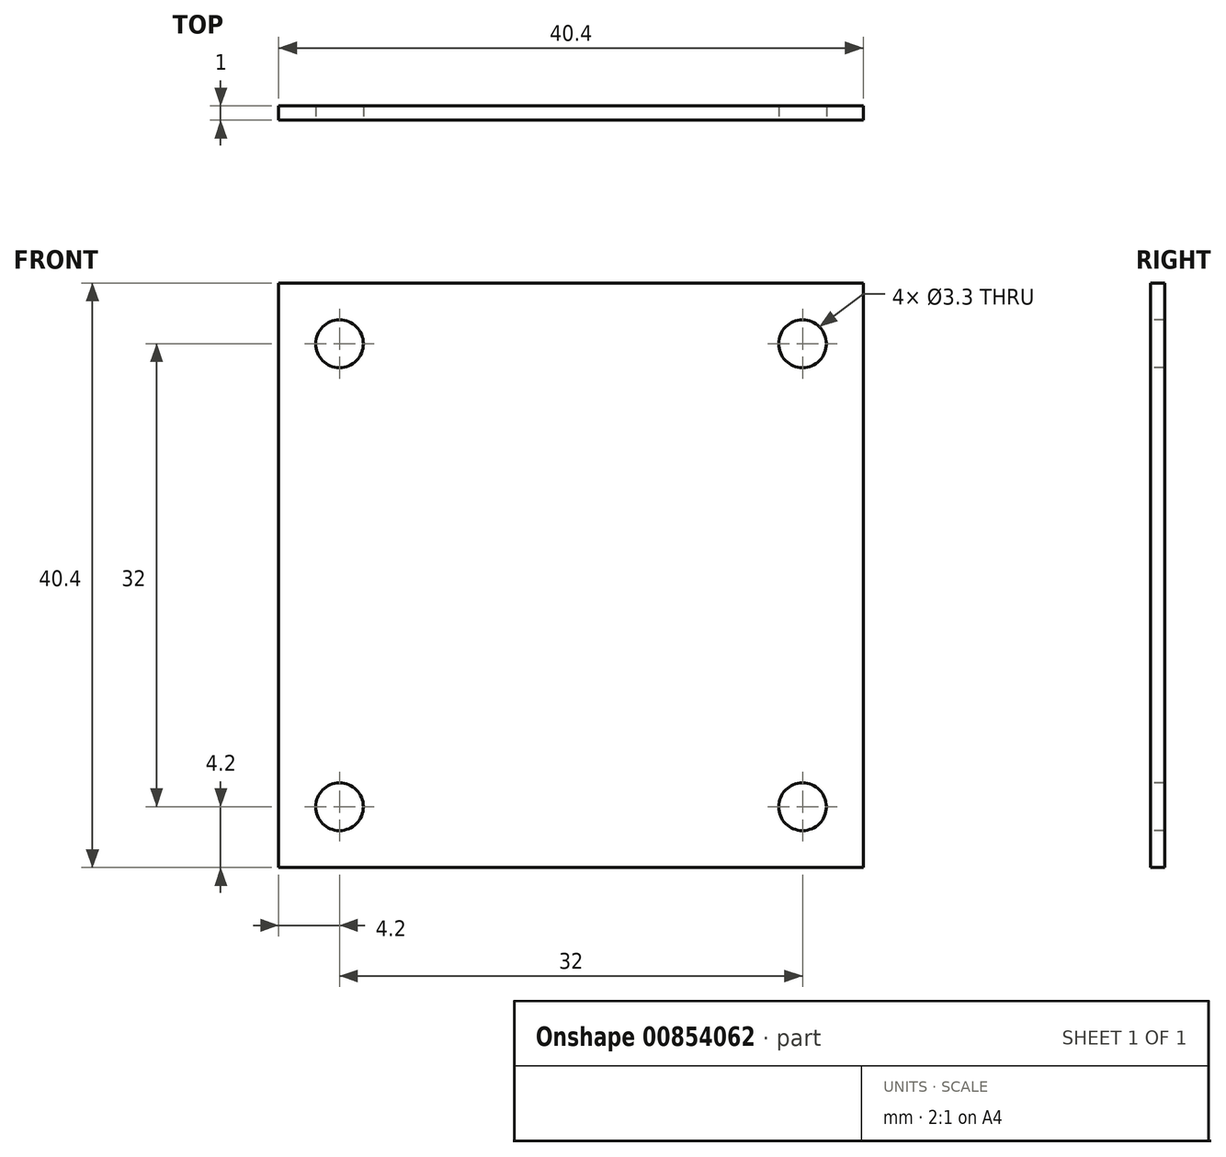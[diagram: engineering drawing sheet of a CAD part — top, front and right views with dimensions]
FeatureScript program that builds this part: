
annotation { "Feature Type Name" : "Feature", "Feature Type Description" : "" }
export const myFeature = defineFeature(function(context is Context, id is Id, definition is map)
    precondition{}
    {
        {
            var Q0;
            Q0=qCreatedBy(makeId("Front.planeOp"),FACE);
            var sketch = newSketch(context, id + "F0", { "sketchPlane" : qUnion([Q0])});
            skLineSegment(sketch, "E0.bottom", {"start": v(0, 0) * mm, "end": v(40.4, 0) * mm});
            skLineSegment(sketch, "E0.top", {"start": v(0, 40.4) * mm, "end": v(40.4, 40.4) * mm});
            skLineSegment(sketch, "E0.left", {"start": v(0, 0) * mm, "end": v(0, 40.4) * mm});
            skLineSegment(sketch, "E0.right", {"start": v(40.4, 0) * mm, "end": v(40.4, 40.4) * mm});
            skSolve(sketch);
        }
        {
            var Q0;
            Q0=makeQuery(id+"F0.imprint","IMPRINT",FACE,{"disambiguationData":[TD([[makeQuery(id+"F0.imprint","IMPRINT",EDGE,{"derivedFrom":sQuery(id+"F0.wireOp",EDGE,"E0.bottom")}),1.0]])]});
            extrude(context, id + "F1", {"entities" : qUnion([Q0]), "depth" : 1 * mm, "offsetDistance" : 25 * mm});
        }
        {
            var Q0;
            Q0=makeQuery(id+"F1.opExtrude","CAP_FACE",FACE,{"disambiguationData":[OSD([sQuery(id+"F0.wireOp",EDGE,"E0.bottom"),sQuery(id+"F0.wireOp",EDGE,"E0.top"),sQuery(id+"F0.wireOp",EDGE,"E0.left"),sQuery(id+"F0.wireOp",EDGE,"E0.right")])],"isStart":false});
            var sketch = newSketch(context, id + "F2", { "sketchPlane" : qUnion([Q0])});
            skPoint(sketch, "E1", {"position": v(36.2, 36.2) * mm});
            skPoint(sketch, "E2", {"position": v(4.2, 36.2) * mm});
            skPoint(sketch, "E3", {"position": v(4.2, 4.2) * mm});
            skPoint(sketch, "E4", {"position": v(36.2, 4.2) * mm});
            skLineSegment(sketch, "E5", {"start": v(20.2, 40.4) * mm, "end": v(20.2, 0) * mm, "construction": true});
            skLineSegment(sketch, "E6", {"start": v(0, 20.2) * mm, "end": v(40.4, 20.2) * mm, "construction": true});
            skSolve(sketch);
        }
        {
            var Q0;
            Q0=sQuery(id+"F2.wireOp",VERTEX,"E2");
            var Q1;
            Q1=sQuery(id+"F2.wireOp",VERTEX,"E1");
            var Q2;
            Q2=sQuery(id+"F2.wireOp",VERTEX,"E4");
            var Q3;
            Q3=sQuery(id+"F2.wireOp",VERTEX,"E3");
            var Q4;
            Q4=makeQuery(id+"F1.opExtrude","SWEPT_BODY",BODY,{"disambiguationData":[OSD([sQuery(id+"F0.wireOp",EDGE,"E0.bottom"),sQuery(id+"F0.wireOp",EDGE,"E0.top"),sQuery(id+"F0.wireOp",EDGE,"E0.left"),sQuery(id+"F0.wireOp",EDGE,"E0.right")])]});
            hole(context, id + "F3", {"style" : HoleStyle.SIMPLE, "endStyle" : HoleEndStyle.THROUGH, "standardTappedOrClearance" : lookupTablePath({ "fit" : "Normal", "standard" : "ISO", "size" : "M3", "type" : "Clearance" }), "standardBlindInLast" : lookupTablePath({ "fit" : "Standard", "standard" : "ISO", "size" : "M3", "type" : "Clearance" }), "holeDiameter" : 3.3 * mm, "majorDiameter" : 5 * mm, "isTappedThrough" : true, "tappedDepth" : 12 * mm, "tapClearance" : 3, "locations" : qUnion([Q0, Q1, Q2, Q3]), "scope" : qUnion([Q4])});
        }
    });
